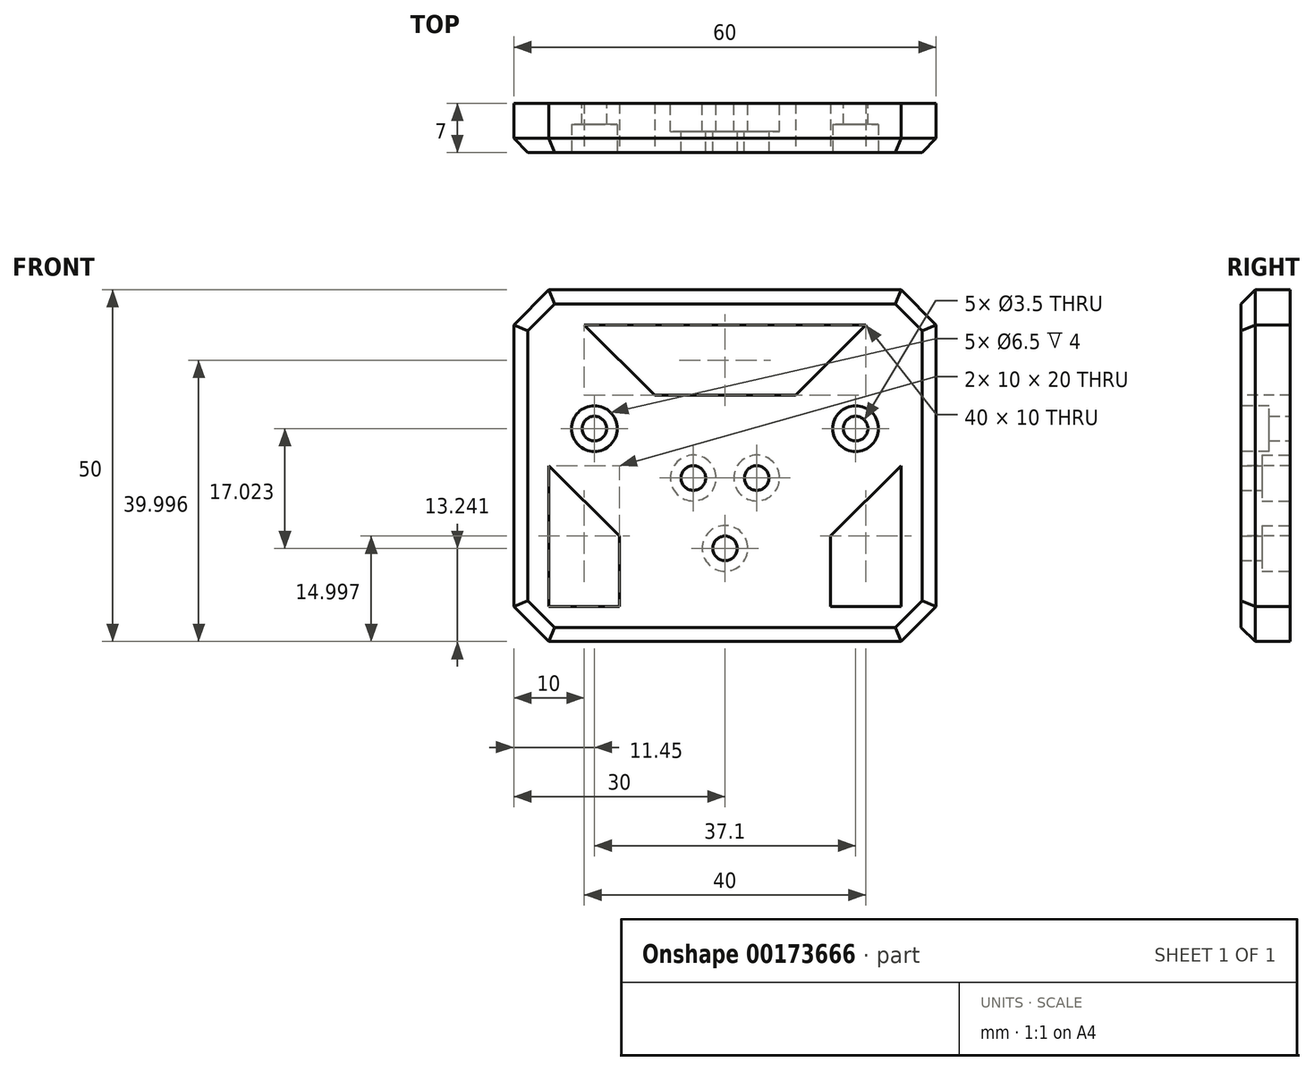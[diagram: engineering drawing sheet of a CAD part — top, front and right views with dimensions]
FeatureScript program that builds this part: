
annotation { "Feature Type Name" : "Feature", "Feature Type Description" : "" }
export const myFeature = defineFeature(function(context is Context, id is Id, definition is map)
    precondition{}
    {
        {
            var Q0;
            Q0=qCreatedBy(makeId("Front.planeOp"),FACE);
            var sketch = newSketch(context, id + "F0", { "sketchPlane" : qUnion([Q0])});
            skLineSegment(sketch, "E0", {"start": v(-30, 0) * mm, "end": v(30, 0) * mm, "construction": true});
            skLineSegment(sketch, "E1", {"start": v(30, 41.75) * mm, "end": v(-30, 41.75) * mm});
            skLineSegment(sketch, "E2", {"start": v(-30, 41.75) * mm, "end": v(-30, -8.25) * mm});
            skLineSegment(sketch, "E3", {"start": v(-30, -8.25) * mm, "end": v(30, -8.25) * mm});
            skLineSegment(sketch, "E4", {"start": v(30, -8.25) * mm, "end": v(30, 41.75) * mm});
            skLineSegment(sketch, "E5", {"start": v(-18.55, 22.01) * mm, "end": v(18.55, 22.01) * mm, "construction": true});
            skPoint(sketch, "E6", {"position": v(0, 22.01) * mm});
            skCircle(sketch, "E7", {"center": v(-18.55, 22.01) * mm, "radius": 1.75 * mm});
            skCircle(sketch, "E8", {"center": v(18.55, 22.01) * mm, "radius": 1.75 * mm});
            skPoint(sketch, "E9", {"position": v(0, 15) * mm});
            skLineSegment(sketch, "E10", {"start": v(-4.5, 15) * mm, "end": v(4.5, 15) * mm, "construction": true});
            skLineSegment(sketch, "E11", {"start": v(0, 15) * mm, "end": v(0, 5) * mm, "construction": true});
            skCircle(sketch, "E12", {"center": v(-4.5, 15) * mm, "radius": 1.75 * mm});
            skCircle(sketch, "E13", {"center": v(4.5, 15) * mm, "radius": 1.75 * mm});
            skCircle(sketch, "E14", {"center": v(0, 5) * mm, "radius": 1.75 * mm});
            skSolve(sketch);
        }
        {
            var Q0;
            Q0=qSketchRegion(id+"F0",true);
            extrude(context, id + "F1", {"entities" : qUnion([Q0]), "depth" : 7 * mm});
        }
        {
            var Q0;
            Q0=makeQuery(id+"F1.opExtrude","SWEPT_EDGE",EDGE,{"disambiguationData":[OSD([sQuery(id+"F0.wireOp",EDGE,"E2"),sQuery(id+"F0.wireOp",EDGE,"E3")])]});
            var Q1;
            Q1=makeQuery(id+"F1.opExtrude","SWEPT_EDGE",EDGE,{"disambiguationData":[OSD([sQuery(id+"F0.wireOp",EDGE,"E3"),sQuery(id+"F0.wireOp",EDGE,"E4")])]});
            var Q2;
            Q2=makeQuery(id+"F1.opExtrude","SWEPT_EDGE",EDGE,{"disambiguationData":[OSD([sQuery(id+"F0.wireOp",EDGE,"E1"),sQuery(id+"F0.wireOp",EDGE,"E4")])]});
            var Q3;
            Q3=makeQuery(id+"F1.opExtrude","SWEPT_EDGE",EDGE,{"disambiguationData":[OSD([sQuery(id+"F0.wireOp",EDGE,"E1"),sQuery(id+"F0.wireOp",EDGE,"E2")])]});
            chamfer(context, id + "F2", {"entities" : qUnion([Q0, Q1, Q2, Q3]), "width" : 5 * mm, "tangentPropagation" : true});
        }
        {
            var Q0;
            Q0=makeQuery(id+"F1.opExtrude","CAP_FACE",FACE,{"disambiguationData":[OSD([sQuery(id+"F0.wireOp",EDGE,"E1"),sQuery(id+"F0.wireOp",EDGE,"E2"),sQuery(id+"F0.wireOp",EDGE,"E3"),sQuery(id+"F0.wireOp",EDGE,"E4"),sQuery(id+"F0.wireOp",EDGE,"E7"),sQuery(id+"F0.wireOp",EDGE,"E8"),sQuery(id+"F0.wireOp",EDGE,"E12"),sQuery(id+"F0.wireOp",EDGE,"E13"),sQuery(id+"F0.wireOp",EDGE,"E14")])],"isStart":true});
            var sketch = newSketch(context, id + "F3", { "sketchPlane" : qUnion([Q0])});
            skCircle(sketch, "E15", {"center": v(-4.5, 15) * mm, "radius": 3.25 * mm});
            skCircle(sketch, "E16", {"center": v(4.5, 15) * mm, "radius": 3.25 * mm});
            skCircle(sketch, "E17", {"center": v(0, 5) * mm, "radius": 3.25 * mm});
            skSolve(sketch);
        }
        {
            var Q0;
            Q0=qSketchRegion(id+"F3",true);
            extrude(context, id + "F4", {"entities" : qUnion([Q0]), "operationType" : NewBodyOperationType.REMOVE, "oppositeDirection" : true, "depth" : 4 * mm});
        }
        {
            var Q0;
            Q0=makeQuery(id+"F1.opExtrude","CAP_FACE",FACE,{"disambiguationData":[OSD([sQuery(id+"F0.wireOp",EDGE,"E1"),sQuery(id+"F0.wireOp",EDGE,"E2"),sQuery(id+"F0.wireOp",EDGE,"E3"),sQuery(id+"F0.wireOp",EDGE,"E4"),sQuery(id+"F0.wireOp",EDGE,"E7"),sQuery(id+"F0.wireOp",EDGE,"E8"),sQuery(id+"F0.wireOp",EDGE,"E12"),sQuery(id+"F0.wireOp",EDGE,"E13"),sQuery(id+"F0.wireOp",EDGE,"E14")])],"isStart":false});
            var sketch = newSketch(context, id + "F5", { "sketchPlane" : qUnion([Q0])});
            skCircle(sketch, "E18", {"center": v(-18.55, 22.01) * mm, "radius": 3.25 * mm});
            skCircle(sketch, "E19", {"center": v(18.55, 22.01) * mm, "radius": 3.25 * mm});
            skSolve(sketch);
        }
        {
            var Q0;
            Q0=qSketchRegion(id+"F5",true);
            extrude(context, id + "F6", {"entities" : qUnion([Q0]), "operationType" : NewBodyOperationType.REMOVE, "oppositeDirection" : true, "depth" : 4 * mm});
        }
        {
            var Q0;
            Q0=makeQuery(id+"F1.opExtrude","CAP_FACE",FACE,{"disambiguationData":[OSD([sQuery(id+"F0.wireOp",EDGE,"E1"),sQuery(id+"F0.wireOp",EDGE,"E2"),sQuery(id+"F0.wireOp",EDGE,"E3"),sQuery(id+"F0.wireOp",EDGE,"E4"),sQuery(id+"F0.wireOp",EDGE,"E7"),sQuery(id+"F0.wireOp",EDGE,"E8"),sQuery(id+"F0.wireOp",EDGE,"E12"),sQuery(id+"F0.wireOp",EDGE,"E13"),sQuery(id+"F0.wireOp",EDGE,"E14")])],"isStart":false});
            var sketch = newSketch(context, id + "F7", { "sketchPlane" : qUnion([Q0])});
            skLineSegment(sketch, "E20", {"start": v(0, 36.75) * mm, "end": v(-20, 36.75) * mm});
            skLineSegment(sketch, "E21", {"start": v(-20, 36.75) * mm, "end": v(-10, 26.75) * mm});
            skLineSegment(sketch, "E22", {"start": v(-10, 26.75) * mm, "end": v(0, 26.75) * mm});
            skLineSegment(sketch, "E23", {"start": v(0, 26.75) * mm, "end": v(10, 26.75) * mm});
            skPoint(sketch, "E23.endSnap0", {"position": v(-5, 26.75) * mm});
            skLineSegment(sketch, "E24", {"start": v(10, 26.75) * mm, "end": v(20, 36.75) * mm});
            skLineSegment(sketch, "E25", {"start": v(20, 36.75) * mm, "end": v(0, 36.75) * mm});
            skLineSegment(sketch, "E26", {"start": v(25, 16.75) * mm, "end": v(25, -3.25) * mm});
            skLineSegment(sketch, "E27", {"start": v(25, -3.25) * mm, "end": v(15, -3.25) * mm});
            skLineSegment(sketch, "E28", {"start": v(15, -3.25) * mm, "end": v(15, 6.75) * mm});
            skLineSegment(sketch, "E29", {"start": v(15, 6.75) * mm, "end": v(25, 16.75) * mm});
            skLineSegment(sketch, "E30", {"start": v(-25, 16.75) * mm, "end": v(-25, -3.25) * mm});
            skLineSegment(sketch, "E31", {"start": v(-25, -3.25) * mm, "end": v(-15, -3.25) * mm});
            skLineSegment(sketch, "E32", {"start": v(-15, -3.25) * mm, "end": v(-15, 6.75) * mm});
            skLineSegment(sketch, "E33", {"start": v(-15, 6.75) * mm, "end": v(-25, 16.75) * mm});
            skSolve(sketch);
        }
        {
            var Q0;
            Q0=qSketchRegion(id+"F7",true);
            extrude(context, id + "F8", {"entities" : qUnion([Q0]), "operationType" : NewBodyOperationType.REMOVE, "endBound" : BoundingType.THROUGH_ALL, "oppositeDirection" : true, "depth" : 25 * mm});
        }
        {
            var Q0;
            Q0=makeQuery(id+"F1.opExtrude","CAP_EDGE",EDGE,{"disambiguationData":[OSD([sQuery(id+"F0.wireOp",EDGE,"E1")])],"isStart":false});
            var Q1;
            {var subQ0=sQuery(id+"F0.wireOp",EDGE,"E4");var subQ1=sQuery(id+"F0.wireOp",EDGE,"E1");Q1=makeQuery(id+"F2.opChamfer","BLEND_EDGE",EDGE,{"blendedFrom":[makeQuery(id+"F1.opExtrude","SWEPT_EDGE",EDGE,{"disambiguationData":[OSD([subQ1,subQ0])]}),makeQuery(id+"F1.opExtrude","CAP_FACE",FACE,{"disambiguationData":[OSD([subQ1,sQuery(id+"F0.wireOp",EDGE,"E2"),sQuery(id+"F0.wireOp",EDGE,"E3"),subQ0,sQuery(id+"F0.wireOp",EDGE,"E7"),sQuery(id+"F0.wireOp",EDGE,"E8"),sQuery(id+"F0.wireOp",EDGE,"E12"),sQuery(id+"F0.wireOp",EDGE,"E13"),sQuery(id+"F0.wireOp",EDGE,"E14")])],"isStart":false})],"blendedInto":[makeQuery(id+"F1.opExtrude","CAP_FACE",FACE,{"disambiguationData":[OSD([subQ1,sQuery(id+"F0.wireOp",EDGE,"E2"),sQuery(id+"F0.wireOp",EDGE,"E3"),subQ0,sQuery(id+"F0.wireOp",EDGE,"E7"),sQuery(id+"F0.wireOp",EDGE,"E8"),sQuery(id+"F0.wireOp",EDGE,"E12"),sQuery(id+"F0.wireOp",EDGE,"E13"),sQuery(id+"F0.wireOp",EDGE,"E14")])],"isStart":false})]});}
            var Q2;
            {var subQ0=sQuery(id+"F0.wireOp",EDGE,"E2");var subQ1=sQuery(id+"F0.wireOp",EDGE,"E1");Q2=makeQuery(id+"F2.opChamfer","BLEND_EDGE",EDGE,{"blendedFrom":[makeQuery(id+"F1.opExtrude","SWEPT_EDGE",EDGE,{"disambiguationData":[OSD([subQ1,subQ0])]}),makeQuery(id+"F1.opExtrude","CAP_FACE",FACE,{"disambiguationData":[OSD([subQ1,subQ0,sQuery(id+"F0.wireOp",EDGE,"E3"),sQuery(id+"F0.wireOp",EDGE,"E4"),sQuery(id+"F0.wireOp",EDGE,"E7"),sQuery(id+"F0.wireOp",EDGE,"E8"),sQuery(id+"F0.wireOp",EDGE,"E12"),sQuery(id+"F0.wireOp",EDGE,"E13"),sQuery(id+"F0.wireOp",EDGE,"E14")])],"isStart":false})],"blendedInto":[makeQuery(id+"F1.opExtrude","CAP_FACE",FACE,{"disambiguationData":[OSD([subQ1,subQ0,sQuery(id+"F0.wireOp",EDGE,"E3"),sQuery(id+"F0.wireOp",EDGE,"E4"),sQuery(id+"F0.wireOp",EDGE,"E7"),sQuery(id+"F0.wireOp",EDGE,"E8"),sQuery(id+"F0.wireOp",EDGE,"E12"),sQuery(id+"F0.wireOp",EDGE,"E13"),sQuery(id+"F0.wireOp",EDGE,"E14")])],"isStart":false})]});}
            var Q3;
            Q3=makeQuery(id+"F1.opExtrude","CAP_EDGE",EDGE,{"disambiguationData":[OSD([sQuery(id+"F0.wireOp",EDGE,"E4")])],"isStart":false});
            var Q4;
            {var subQ0=sQuery(id+"F0.wireOp",EDGE,"E4");var subQ1=sQuery(id+"F0.wireOp",EDGE,"E3");Q4=makeQuery(id+"F2.opChamfer","BLEND_EDGE",EDGE,{"blendedFrom":[makeQuery(id+"F1.opExtrude","SWEPT_EDGE",EDGE,{"disambiguationData":[OSD([subQ1,subQ0])]}),makeQuery(id+"F1.opExtrude","CAP_FACE",FACE,{"disambiguationData":[OSD([sQuery(id+"F0.wireOp",EDGE,"E1"),sQuery(id+"F0.wireOp",EDGE,"E2"),subQ1,subQ0,sQuery(id+"F0.wireOp",EDGE,"E7"),sQuery(id+"F0.wireOp",EDGE,"E8"),sQuery(id+"F0.wireOp",EDGE,"E12"),sQuery(id+"F0.wireOp",EDGE,"E13"),sQuery(id+"F0.wireOp",EDGE,"E14")])],"isStart":false})],"blendedInto":[makeQuery(id+"F1.opExtrude","CAP_FACE",FACE,{"disambiguationData":[OSD([sQuery(id+"F0.wireOp",EDGE,"E1"),sQuery(id+"F0.wireOp",EDGE,"E2"),subQ1,subQ0,sQuery(id+"F0.wireOp",EDGE,"E7"),sQuery(id+"F0.wireOp",EDGE,"E8"),sQuery(id+"F0.wireOp",EDGE,"E12"),sQuery(id+"F0.wireOp",EDGE,"E13"),sQuery(id+"F0.wireOp",EDGE,"E14")])],"isStart":false})]});}
            var Q5;
            Q5=makeQuery(id+"F1.opExtrude","CAP_EDGE",EDGE,{"disambiguationData":[OSD([sQuery(id+"F0.wireOp",EDGE,"E3")])],"isStart":false});
            var Q6;
            {var subQ0=sQuery(id+"F0.wireOp",EDGE,"E3");var subQ1=sQuery(id+"F0.wireOp",EDGE,"E2");Q6=makeQuery(id+"F2.opChamfer","BLEND_EDGE",EDGE,{"blendedFrom":[makeQuery(id+"F1.opExtrude","SWEPT_EDGE",EDGE,{"disambiguationData":[OSD([subQ1,subQ0])]}),makeQuery(id+"F1.opExtrude","CAP_FACE",FACE,{"disambiguationData":[OSD([sQuery(id+"F0.wireOp",EDGE,"E1"),subQ1,subQ0,sQuery(id+"F0.wireOp",EDGE,"E4"),sQuery(id+"F0.wireOp",EDGE,"E7"),sQuery(id+"F0.wireOp",EDGE,"E8"),sQuery(id+"F0.wireOp",EDGE,"E12"),sQuery(id+"F0.wireOp",EDGE,"E13"),sQuery(id+"F0.wireOp",EDGE,"E14")])],"isStart":false})],"blendedInto":[makeQuery(id+"F1.opExtrude","CAP_FACE",FACE,{"disambiguationData":[OSD([sQuery(id+"F0.wireOp",EDGE,"E1"),subQ1,subQ0,sQuery(id+"F0.wireOp",EDGE,"E4"),sQuery(id+"F0.wireOp",EDGE,"E7"),sQuery(id+"F0.wireOp",EDGE,"E8"),sQuery(id+"F0.wireOp",EDGE,"E12"),sQuery(id+"F0.wireOp",EDGE,"E13"),sQuery(id+"F0.wireOp",EDGE,"E14")])],"isStart":false})]});}
            var Q7;
            Q7=makeQuery(id+"F1.opExtrude","CAP_EDGE",EDGE,{"disambiguationData":[OSD([sQuery(id+"F0.wireOp",EDGE,"E2")])],"isStart":false});
            chamfer(context, id + "F9", {"entities" : qUnion([Q0, Q1, Q2, Q3, Q4, Q5, Q6, Q7]), "width" : 2 * mm, "tangentPropagation" : true});
        }
    });
